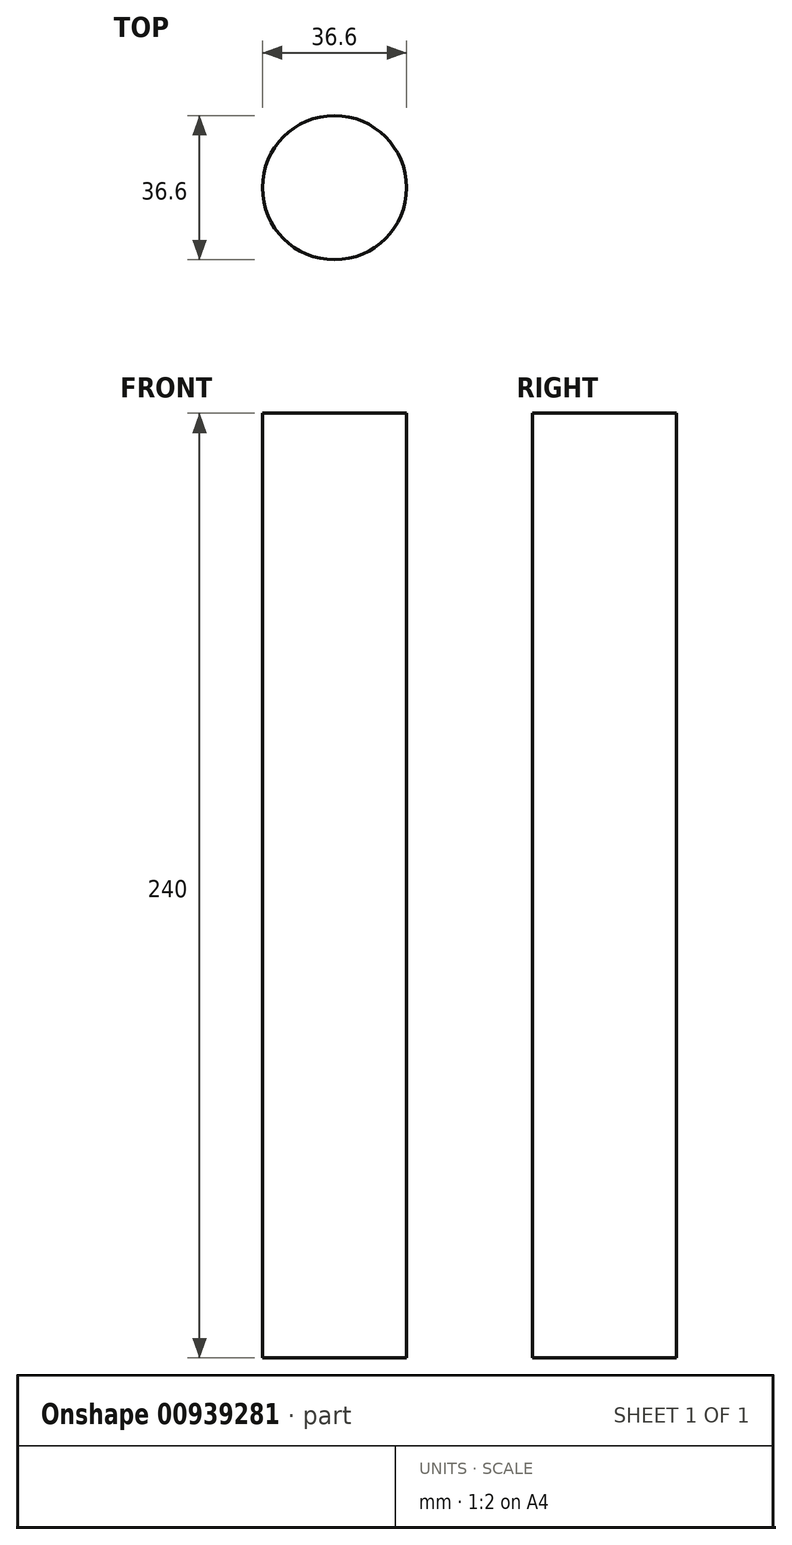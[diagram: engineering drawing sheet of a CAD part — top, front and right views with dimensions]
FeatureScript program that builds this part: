
annotation { "Feature Type Name" : "Feature", "Feature Type Description" : "" }
export const myFeature = defineFeature(function(context is Context, id is Id, definition is map)
    precondition{}
    {
        {
            var Q0;
            Q0=qCreatedBy(makeId("Top.planeOp"),FACE);
            var sketch = newSketch(context, id + "F0", { "sketchPlane" : qUnion([Q0])});
            skCircle(sketch, "E0", {"center": v(0, 0) * mm, "radius": 18.3 * mm});
            skSolve(sketch);
        }
        {
            var Q0;
            Q0=makeQuery(id+"F0.imprint","IMPRINT",FACE,{"disambiguationData":[TD([[makeQuery(id+"F0.imprint","IMPRINT",EDGE,{"derivedFrom":sQuery(id+"F0.wireOp",EDGE,"E0")}),1.0]])]});
            extrude(context, id + "F1", {"entities" : qUnion([Q0]), "depth" : 240 * mm, "offsetDistance" : 25.4 * mm});
        }
    });
